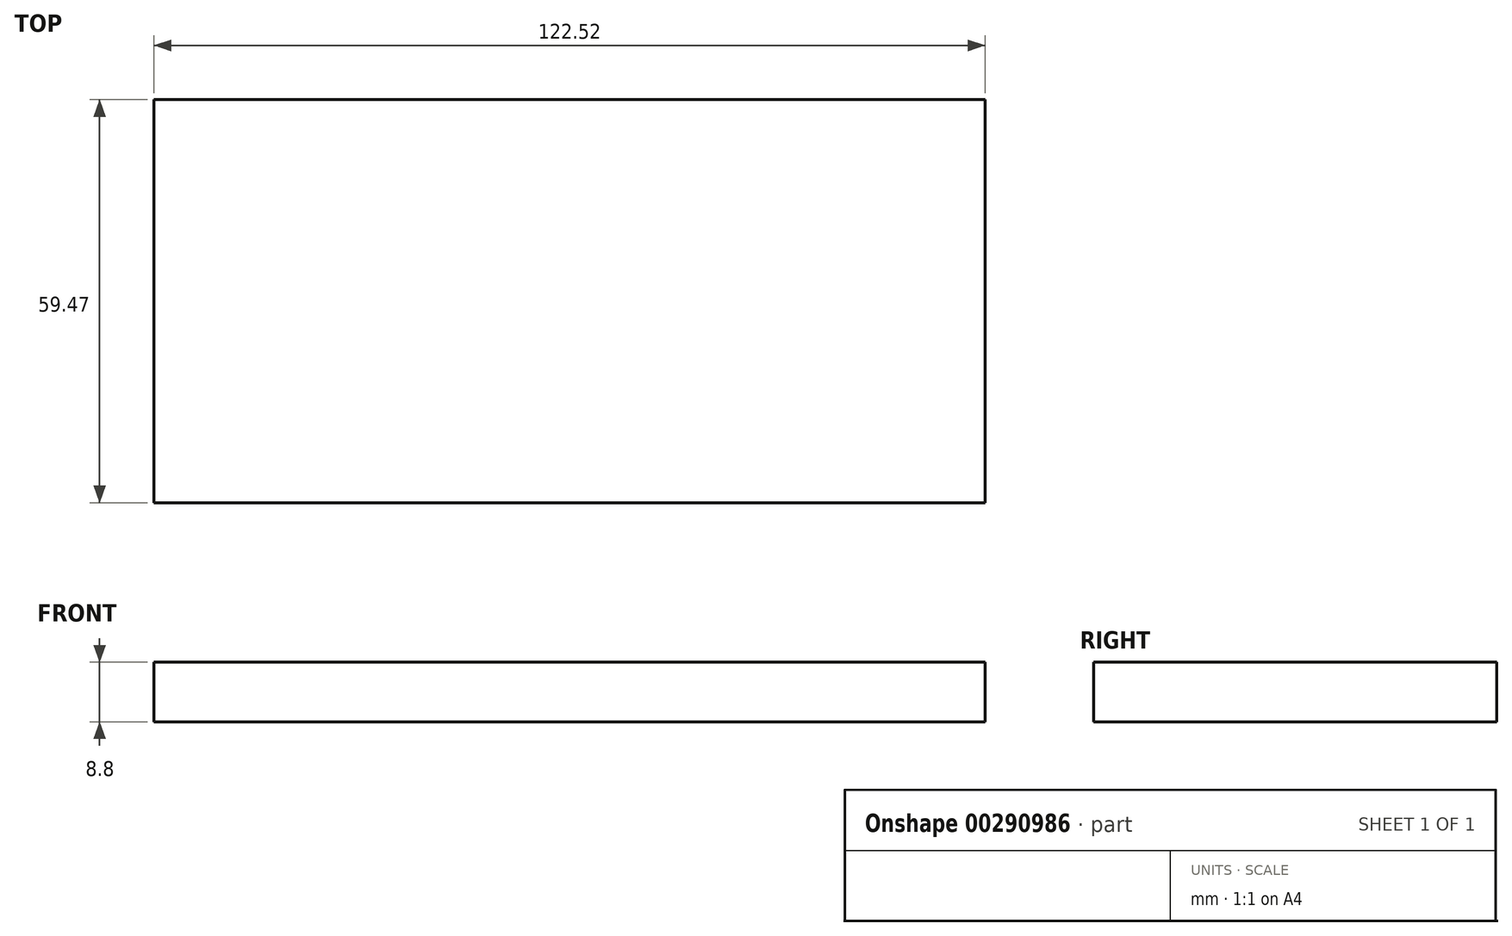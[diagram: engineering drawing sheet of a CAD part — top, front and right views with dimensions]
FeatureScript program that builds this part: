
annotation { "Feature Type Name" : "Feature", "Feature Type Description" : "" }
export const myFeature = defineFeature(function(context is Context, id is Id, definition is map)
    precondition{}
    {
        {
            var Q0;
            Q0=qCreatedBy(makeId("Top.planeOp"),FACE);
            var sketch = newSketch(context, id + "F0", { "sketchPlane" : qUnion([Q0])});
            skLineSegment(sketch, "E0.bottom", {"start": v(0, 0) * mm, "end": v(122.52, 0) * mm});
            skLineSegment(sketch, "E0.top", {"start": v(0, 59.47) * mm, "end": v(122.52, 59.47) * mm});
            skLineSegment(sketch, "E0.left", {"start": v(0, 0) * mm, "end": v(0, 59.47) * mm});
            skLineSegment(sketch, "E0.right", {"start": v(122.52, 0) * mm, "end": v(122.52, 59.47) * mm});
            skSolve(sketch);
        }
        {
            var Q0;
            Q0 = qSketchRegion(id + "F0", true);
            extrude(context, id + "F1", {"entities" : qUnion([Q0]), "depth" : 8.8 * mm});
        }
    });
